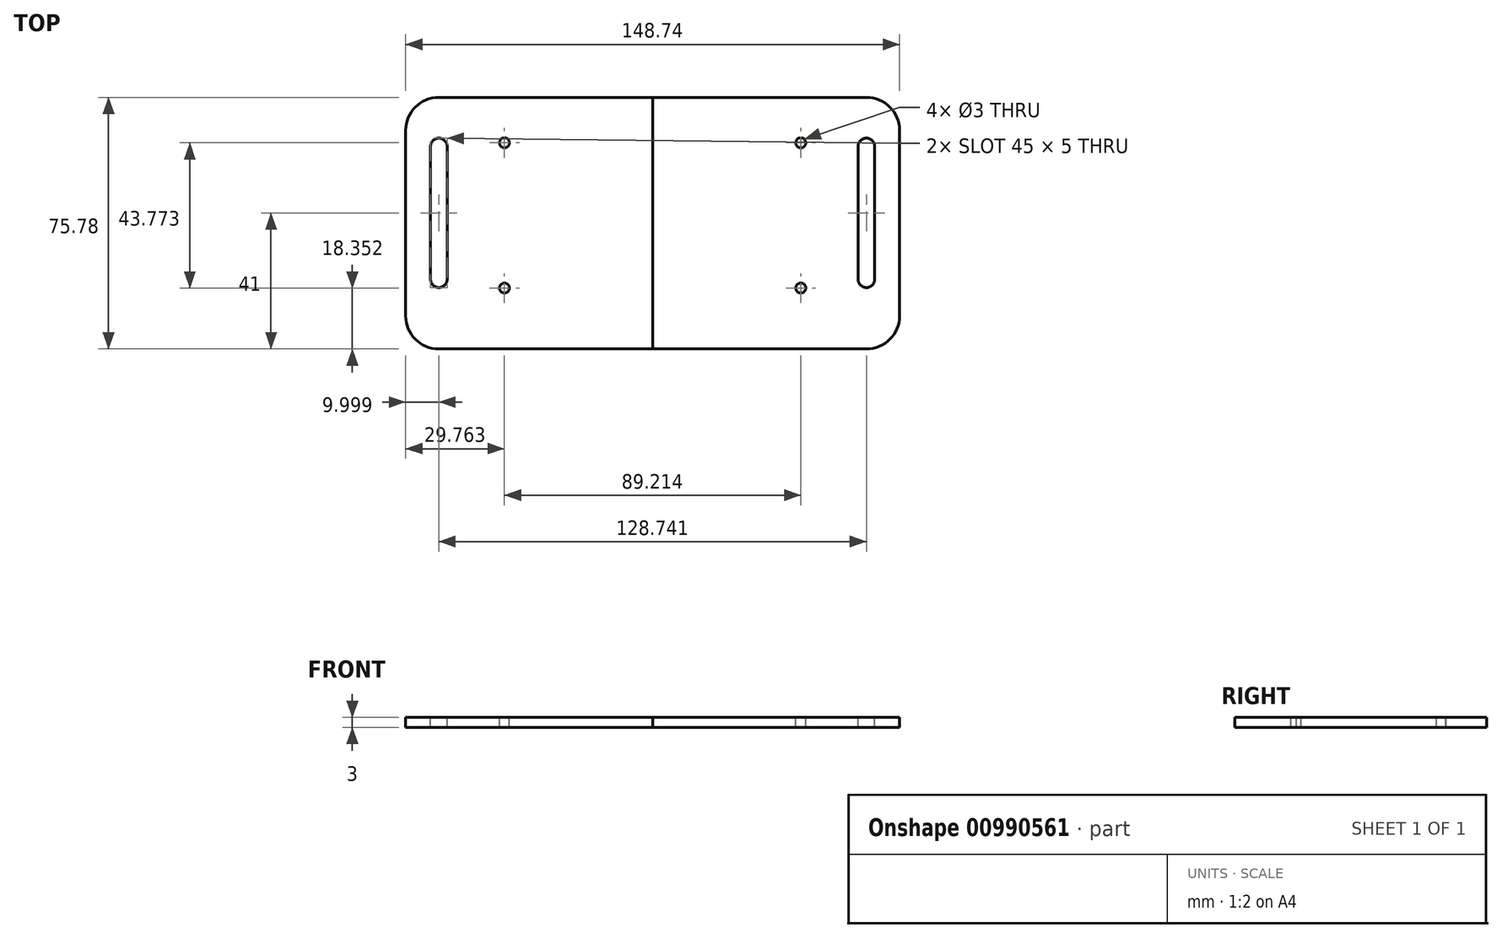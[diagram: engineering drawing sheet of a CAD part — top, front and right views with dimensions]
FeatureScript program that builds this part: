
annotation { "Feature Type Name" : "Feature", "Feature Type Description" : "" }
export const myFeature = defineFeature(function(context is Context, id is Id, definition is map)
    precondition{}
    {
        {
            var Q0;
            Q0=qCreatedBy(makeId("Top.planeOp"),FACE);
            var sketch = newSketch(context, id + "F0", { "sketchPlane" : qUnion([Q0])});
            skLineSegment(sketch, "E0.bottom", {"start": v(0, 0) * mm, "end": v(74.37, 0) * mm});
            skLineSegment(sketch, "E0.top", {"start": v(0, 75.78) * mm, "end": v(74.37, 75.78) * mm});
            skLineSegment(sketch, "E0.left", {"start": v(0, 0) * mm, "end": v(0, 75.78) * mm});
            skLineSegment(sketch, "E0.right", {"start": v(74.37, 0) * mm, "end": v(74.37, 75.78) * mm});
            skSolve(sketch);
        }
        {
            var Q0;
            Q0=makeQuery(id+"F0.imprint","IMPRINT",FACE,{"disambiguationData":[TD([[makeQuery(id+"F0.imprint","IMPRINT",EDGE,{"derivedFrom":sQuery(id+"F0.wireOp",EDGE,"E0.bottom")}),1.0]])]});
            extrude(context, id + "F1", {"entities" : qUnion([Q0]), "depth" : 3 * mm, "offsetDistance" : 25 * mm});
        }
        {
            var Q0;
            Q0=makeQuery(id+"F1.opExtrude","CAP_FACE",FACE,{"disambiguationData":[OSD([sQuery(id+"F0.wireOp",EDGE,"E0.bottom"),sQuery(id+"F0.wireOp",EDGE,"E0.top"),sQuery(id+"F0.wireOp",EDGE,"E0.left"),sQuery(id+"F0.wireOp",EDGE,"E0.right")])],"isStart":false});
            var sketch = newSketch(context, id + "F2", { "sketchPlane" : qUnion([Q0])});
            skLineSegment(sketch, "E1", {"start": v(44.6, 18.35) * mm, "end": v(44.6, 62.12) * mm});
            skSolve(sketch);
        }
        {
            var Q0;
            Q0=sQuery(id+"F2.wireOp",VERTEX,"E1.end");
            var Q1;
            Q1=sQuery(id+"F2.wireOp",VERTEX,"E1.start");
            var Q2;
            Q2=makeQuery(id+"F1.opExtrude","SWEPT_BODY",BODY,{"disambiguationData":[OSD([sQuery(id+"F0.wireOp",EDGE,"E0.bottom"),sQuery(id+"F0.wireOp",EDGE,"E0.top"),sQuery(id+"F0.wireOp",EDGE,"E0.left"),sQuery(id+"F0.wireOp",EDGE,"E0.right")])]});
            hole(context, id + "F3", {"style" : HoleStyle.SIMPLE, "endStyle" : HoleEndStyle.THROUGH, "holeDiameter" : 3 * mm, "majorDiameter" : 5 * mm, "isTappedThrough" : true, "tappedDepth" : 12 * mm, "tapClearance" : 3, "locations" : qUnion([Q0, Q1]), "scope" : qUnion([Q2])});
        }
        {
            var Q0;
            Q0=makeQuery(id+"F1.opExtrude","CAP_FACE",FACE,{"disambiguationData":[OSD([sQuery(id+"F0.wireOp",EDGE,"E0.bottom"),sQuery(id+"F0.wireOp",EDGE,"E0.top"),sQuery(id+"F0.wireOp",EDGE,"E0.left"),sQuery(id+"F0.wireOp",EDGE,"E0.right")])],"isStart":false});
            var sketch = newSketch(context, id + "F4", { "sketchPlane" : qUnion([Q0])});
            skLineSegment(sketch, "E2", {"start": v(64.37, 21) * mm, "end": v(64.37, 61) * mm});
            skArc(sketch, "E3.0.startCap", {"start": v(66.87, 21) * mm, "mid": v(64.37, 18.5) * mm, "end": v(61.87, 21) * mm});
            skArc(sketch, "E3.0.endCap", {"start": v(61.87, 61) * mm, "mid": v(64.37, 63.5) * mm, "end": v(66.87, 61) * mm});
            skLineSegment(sketch, "E3.0.left", {"start": v(61.87, 21) * mm, "end": v(61.87, 61) * mm});
            skLineSegment(sketch, "E3.0.right", {"start": v(66.87, 21) * mm, "end": v(66.87, 61) * mm});
            skSolve(sketch);
        }
        {
            var Q0;
            Q0=makeQuery(id+"F4.imprint","IMPRINT",FACE,{"disambiguationData":[TD([[makeQuery(id+"F4.imprint","IMPRINT",EDGE,{"derivedFrom":sQuery(id+"F4.wireOp",EDGE,"E3.0.startCap")}),-1.0]])]});
            var sketch = newSketch(context, id + "F5", { "sketchPlane" : qUnion([Q0])});
            skLineSegment(sketch, "E4.JUB.JUB", {"start": v(64.37, 21) * mm, "end": v(64.37, 61) * mm, "construction": true});
            skArc(sketch, "E4.0.startCap", {"start": v(66.87, 21) * mm, "mid": v(64.37, 18.5) * mm, "end": v(61.87, 21) * mm});
            skArc(sketch, "E4.0.endCap", {"start": v(61.87, 61) * mm, "mid": v(64.37, 63.5) * mm, "end": v(66.87, 61) * mm});
            skLineSegment(sketch, "E4.0.left", {"start": v(61.87, 21) * mm, "end": v(61.87, 61) * mm});
            skLineSegment(sketch, "E4.0.right", {"start": v(66.87, 21) * mm, "end": v(66.87, 61) * mm});
            skSolve(sketch);
        }
        {
            var Q0;
            Q0 = qSketchRegion(id + "F5", true);
            extrude(context, id + "F6", {"entities" : qUnion([Q0]), "operationType" : NewBodyOperationType.REMOVE, "oppositeDirection" : true, "depth" : 77.58 * mm, "offsetDistance" : 25 * mm});
        }
        {
            var Q0;
            Q0=makeQuery(id+"F1.opExtrude","SWEPT_EDGE",EDGE,{"disambiguationData":[OSD([sQuery(id+"F0.wireOp",EDGE,"E0.bottom"),sQuery(id+"F0.wireOp",EDGE,"E0.right")])]});
            var Q1;
            Q1=makeQuery(id+"F1.opExtrude","SWEPT_EDGE",EDGE,{"disambiguationData":[OSD([sQuery(id+"F0.wireOp",EDGE,"E0.top"),sQuery(id+"F0.wireOp",EDGE,"E0.right")])]});
            fillet(context, id + "F7", {"entities" : qUnion([Q0, Q1]), "radius" : 10 * mm, "tangentPropagation" : true, "allowEdgeOverflow" : false});
        }
        {
            var Q0;
            Q0=makeQuery(id+"F1.opExtrude","SWEPT_BODY",BODY,{"disambiguationData":[OSD([sQuery(id+"F0.wireOp",EDGE,"E0.bottom"),sQuery(id+"F0.wireOp",EDGE,"E0.top"),sQuery(id+"F0.wireOp",EDGE,"E0.left"),sQuery(id+"F0.wireOp",EDGE,"E0.right")])]});
            var Q1;
            Q1=qCreatedBy(makeId("Right.planeOp"),FACE);
            mirror(context, id + "F8", {"entities" : qUnion([Q0]), "mirrorPlane" : qUnion([Q1])});
        }
    });
